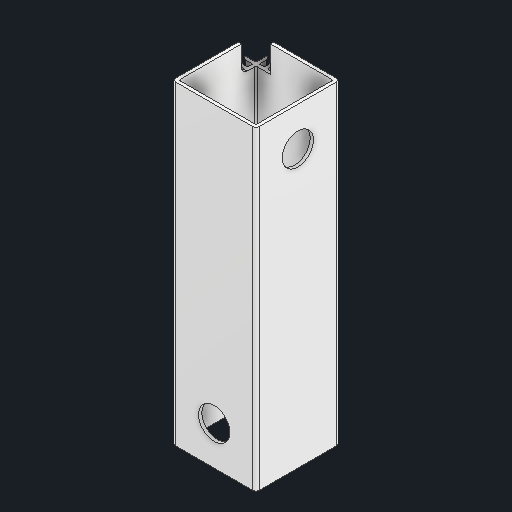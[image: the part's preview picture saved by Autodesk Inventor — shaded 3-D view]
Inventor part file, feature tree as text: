
AUTODESK INVENTOR PART (.ipt)
format: ipt  version: 2024.2 (Build 282272000, 272)  size: 143,360 bytes
history: native  units: in
note: dims shown in document units (in); Inventor stores cm internally (conversion verified against a paired STEP export)
features: fillet x1
ambient origin geometry x8: Origin, YZ Plane, XZ Plane, XY Plane, X Axis, Y Axis, Z Axis, Center Point
bodies: Solid1 (feature_tree)
feature tree (1):
  fillet  "Fillet5"  [1 undecoded]
note: 1 required parameter value undecoded (feature->parameter linkage not recoverable at this tier; creation-order binding heuristic only, values carry confidence <= 0.55)
